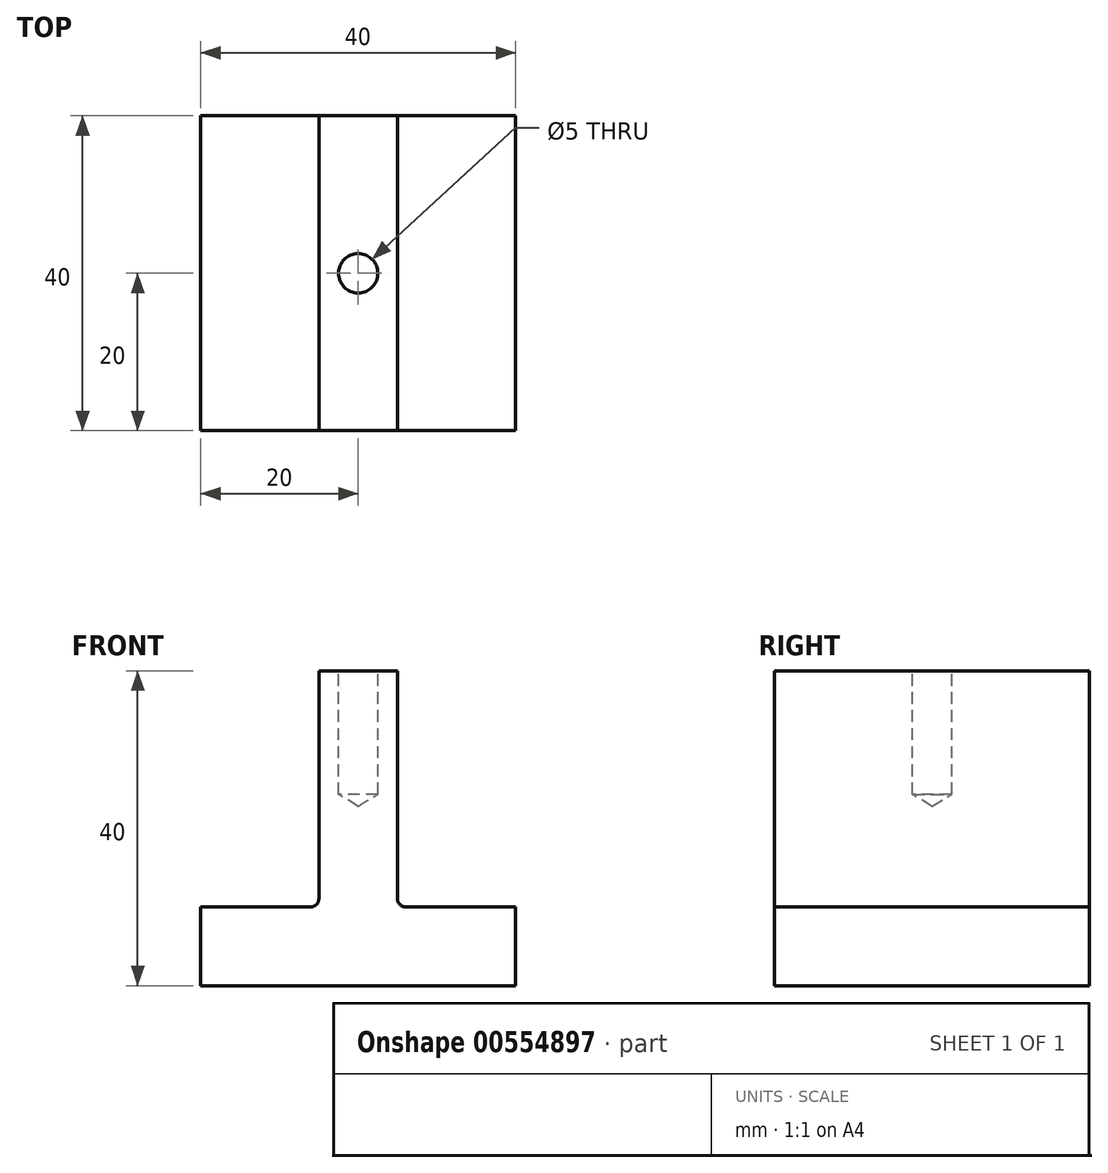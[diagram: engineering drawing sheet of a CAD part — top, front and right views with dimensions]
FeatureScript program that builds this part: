
annotation { "Feature Type Name" : "Feature", "Feature Type Description" : "" }
export const myFeature = defineFeature(function(context is Context, id is Id, definition is map)
    precondition{}
    {
        {
            var Q0;
            Q0=qCreatedBy(makeId("Front.planeOp"),FACE);
            var sketch = newSketch(context, id + "F0", { "sketchPlane" : qUnion([Q0])});
            skLineSegment(sketch, "E0", {"start": v(-5, 30) * mm, "end": v(-5, 0) * mm});
            skLineSegment(sketch, "E1", {"start": v(-5, 0) * mm, "end": v(-20, 0) * mm});
            skLineSegment(sketch, "E2", {"start": v(-20, 0) * mm, "end": v(-20, -10) * mm});
            skLineSegment(sketch, "E3", {"start": v(-20, -10) * mm, "end": v(20, -10) * mm});
            skLineSegment(sketch, "E4", {"start": v(20, -10) * mm, "end": v(20, 0) * mm});
            skLineSegment(sketch, "E5", {"start": v(20, 0) * mm, "end": v(5, 0) * mm});
            skLineSegment(sketch, "E6", {"start": v(5, 0) * mm, "end": v(5, 30) * mm});
            skLineSegment(sketch, "E7", {"start": v(5, 30) * mm, "end": v(-5, 30) * mm});
            skSolve(sketch);
        }
        {
            var Q0;
            Q0=makeQuery(id+"F0.imprint","IMPRINT",FACE,{"disambiguationData":[TD([[makeQuery(id+"F0.imprint","IMPRINT",EDGE,{"derivedFrom":sQuery(id+"F0.wireOp",EDGE,"E0")}),1.0]])]});
            extrude(context, id + "F1", {"entities" : qUnion([Q0]), "endBound" : BoundingType.SYMMETRIC, "depth" : 40 * mm, "offsetDistance" : 25.4 * mm});
        }
        {
            var Q0;
            Q0=makeQuery(id+"F1.opExtrude","SWEPT_FACE",FACE,{"disambiguationData":[OSD([sQuery(id+"F0.wireOp",EDGE,"E7")])]});
            var sketch = newSketch(context, id + "F2", { "sketchPlane" : qUnion([Q0])});
            skPoint(sketch, "E8", {"position": v(0, 0) * mm});
            skSolve(sketch);
        }
        {
            var Q0;
            Q0=sQuery(id+"F2.wireOp",VERTEX,"E8");
            var Q1;
            Q1=makeQuery(id+"F1.opExtrude","SWEPT_BODY",BODY,{"disambiguationData":[OSD([sQuery(id+"F0.wireOp",EDGE,"E0"),sQuery(id+"F0.wireOp",EDGE,"E1"),sQuery(id+"F0.wireOp",EDGE,"E2"),sQuery(id+"F0.wireOp",EDGE,"E3"),sQuery(id+"F0.wireOp",EDGE,"E4"),sQuery(id+"F0.wireOp",EDGE,"E5"),sQuery(id+"F0.wireOp",EDGE,"E6"),sQuery(id+"F0.wireOp",EDGE,"E7")])]});
            hole(context, id + "F3", {"style" : HoleStyle.SIMPLE, "endStyle" : HoleEndStyle.BLIND, "standardTappedOrClearance" : lookupTablePath({ "standard" : "ISO", "engagement" : "75%", "pitch" : "1 mm", "size" : "M6", "type" : "Tapped" }), "standardBlindInLast" : lookupTablePath({ "standard" : "ISO", "engagement" : "75%", "pitch" : "1 mm", "size" : "M6", "type" : "Tapped" }), "holeDiameter" : 5 * mm, "showTappedDepth" : true, "holeDepth" : 15.7 * mm, "isTappedThrough" : true, "tappedDepth" : 12.7 * mm, "tapClearance" : 3, "locations" : qUnion([Q0]), "scope" : qUnion([Q1]), "majorDiameter" : 6 * mm});
        }
        {
            var Q0;
            Q0=makeQuery(id+"F1.opExtrude","SWEPT_EDGE",EDGE,{"disambiguationData":[OSD([sQuery(id+"F0.wireOp",EDGE,"E5"),sQuery(id+"F0.wireOp",EDGE,"E6")])]});
            var Q1;
            Q1=makeQuery(id+"F1.opExtrude","SWEPT_EDGE",EDGE,{"disambiguationData":[OSD([sQuery(id+"F0.wireOp",EDGE,"E0"),sQuery(id+"F0.wireOp",EDGE,"E1")])]});
            fillet(context, id + "F4", {"entities" : qUnion([Q0, Q1]), "radius" : 1 * mm, "tangentPropagation" : true, "allowEdgeOverflow" : false});
        }
    });
